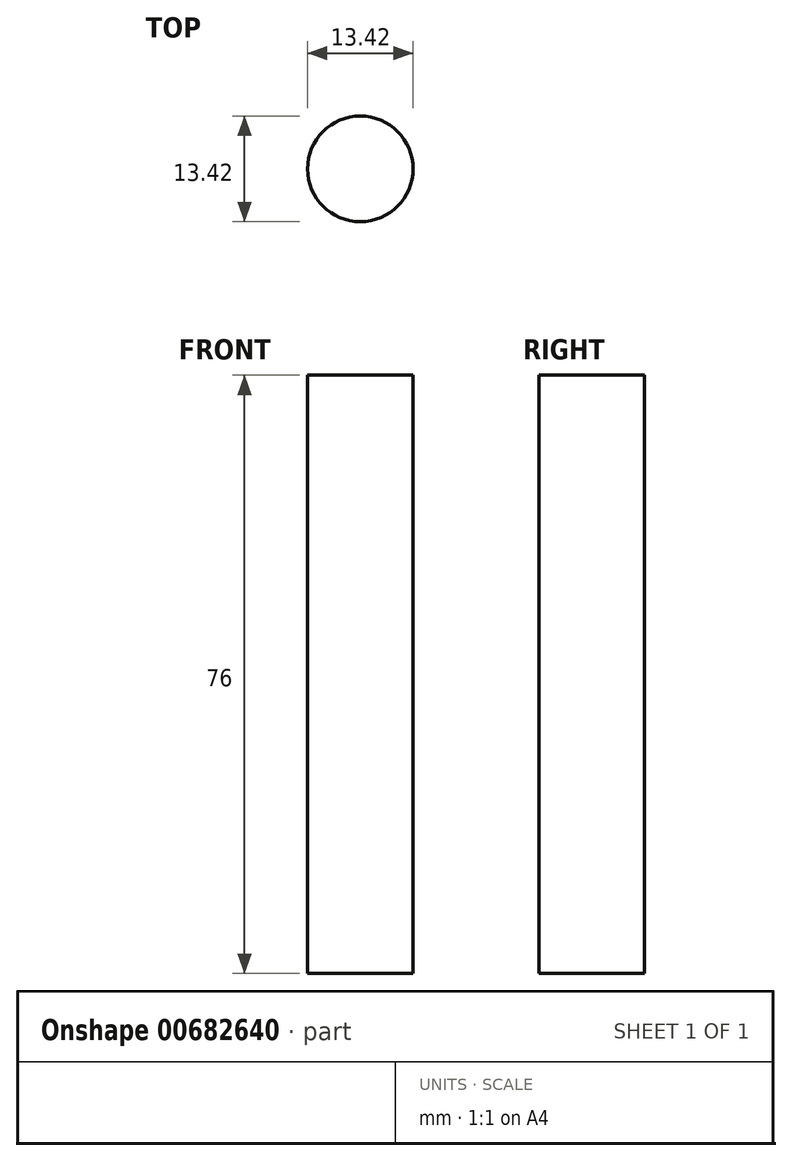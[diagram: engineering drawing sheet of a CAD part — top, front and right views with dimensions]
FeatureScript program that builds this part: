
annotation { "Feature Type Name" : "Feature", "Feature Type Description" : "" }
export const myFeature = defineFeature(function(context is Context, id is Id, definition is map)
    precondition{}
    {
        {
            var Q0;
            Q0=qCreatedBy(makeId("Top.planeOp"),FACE);
            var sketch = newSketch(context, id + "F0", { "sketchPlane" : qUnion([Q0])});
            skCircle(sketch, "E0", {"center": v(0, 0) * mm, "radius": 6.7 * mm});
            skSolve(sketch);
        }
        {
            var Q0;
            Q0 = qSketchRegion(id + "F0", true);
            extrude(context, id + "F1", {"entities" : qUnion([Q0]), "depth" : 76 * mm, "offsetDistance" : 25 * mm});
        }
    });
